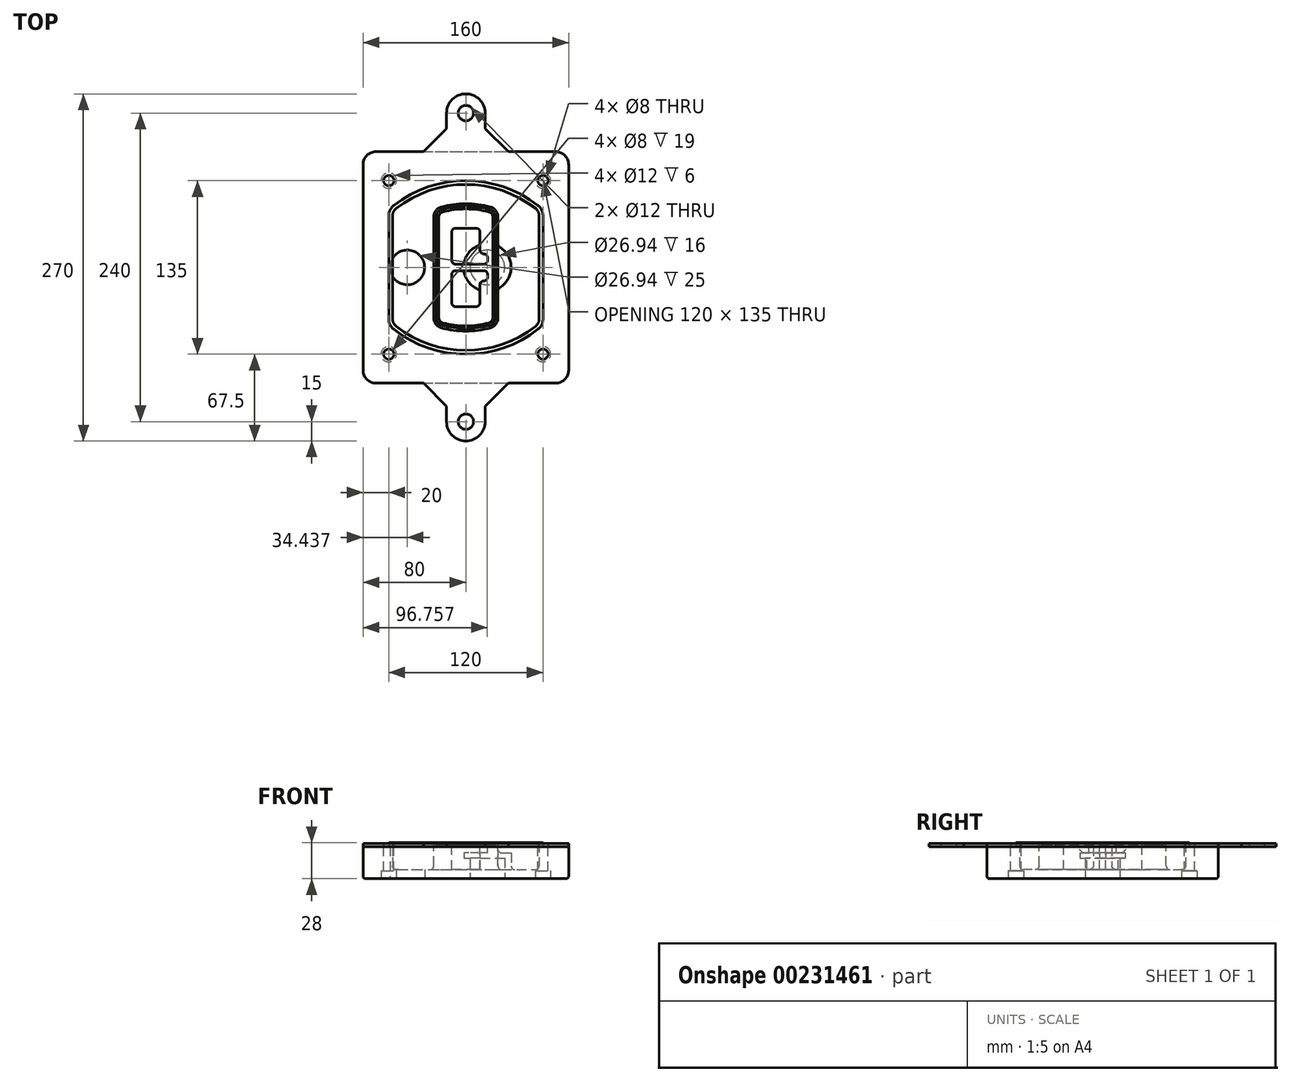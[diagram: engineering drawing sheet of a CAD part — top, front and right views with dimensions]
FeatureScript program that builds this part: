
annotation { "Feature Type Name" : "Feature", "Feature Type Description" : "" }
export const myFeature = defineFeature(function(context is Context, id is Id, definition is map)
    precondition{}
    {
        {
            var Q0;
            Q0=qCreatedBy(makeId("Top.planeOp"),FACE);
            var sketch = newSketch(context, id + "F0", { "sketchPlane" : qUnion([Q0])});
            skPoint(sketch, "E0.rect.middle", {"position": v(0, 0) * mm});
            skLineSegment(sketch, "E1.bottom", {"start": v(-70, -90) * mm, "end": v(70, -90) * mm});
            skLineSegment(sketch, "E1.top", {"start": v(-70, 90) * mm, "end": v(70, 90) * mm});
            skLineSegment(sketch, "E1.left", {"start": v(-80, -80) * mm, "end": v(-80, 80) * mm});
            skLineSegment(sketch, "E1.right", {"start": v(80, -80) * mm, "end": v(80, 80) * mm});
            skLineSegment(sketch, "E2", {"start": v(-80, 90) * mm, "end": v(80, -90) * mm, "construction": true});
            skLineSegment(sketch, "E3", {"start": v(80, 90) * mm, "end": v(-80, -90) * mm, "construction": true});
            skCircle(sketch, "E4", {"center": v(-60, 67.5) * mm, "radius": 4 * mm});
            skCircle(sketch, "E5", {"center": v(60, 67.5) * mm, "radius": 4 * mm});
            skCircle(sketch, "E6", {"center": v(60, -67.5) * mm, "radius": 4 * mm});
            skCircle(sketch, "E7", {"center": v(-60, -67.5) * mm, "radius": 4 * mm});
            skLineSegment(sketch, "E8", {"start": v(-60, 67.5) * mm, "end": v(60, 67.5) * mm, "construction": true});
            skLineSegment(sketch, "E9", {"start": v(60, 67.5) * mm, "end": v(60, -67.5) * mm, "construction": true});
            skLineSegment(sketch, "E10", {"start": v(60, -67.5) * mm, "end": v(-60, -67.5) * mm, "construction": true});
            skLineSegment(sketch, "E11", {"start": v(-60, -67.5) * mm, "end": v(-60, 67.5) * mm, "construction": true});
            skLineSegment(sketch, "E12", {"start": v(-60, 40.3) * mm, "end": v(-60, -40.3) * mm});
            skLineSegment(sketch, "E13", {"start": v(60, 40.3) * mm, "end": v(60, -40.3) * mm});
            skArc(sketch, "E14", {"start": v(56.15, 48.18) * mm, "mid": v(0, 67.5) * mm, "end": v(-56.15, 48.18) * mm});
            skArc(sketch, "E15", {"start": v(-56.15, -48.18) * mm, "mid": v(0, -67.5) * mm, "end": v(56.15, -48.18) * mm});
            skLineSegment(sketch, "E16", {"start": v(-60, 0) * mm, "end": v(60, 0) * mm, "construction": true});
            skPoint(sketch, "E17.visualSharp", {"position": v(-60, -45) * mm});
            skArc(sketch, "E17.filletArc", {"start": v(-60, -40.3) * mm, "mid": v(-58.99, -44.68) * mm, "end": v(-56.15, -48.18) * mm});
            skPoint(sketch, "E18.visualSharp", {"position": v(-60, 45) * mm});
            skArc(sketch, "E18.filletArc", {"start": v(-56.15, 48.18) * mm, "mid": v(-58.99, 44.68) * mm, "end": v(-60, 40.3) * mm});
            skPoint(sketch, "E19.visualSharp", {"position": v(60, 45) * mm});
            skArc(sketch, "E19.filletArc", {"start": v(60, 40.3) * mm, "mid": v(58.99, 44.68) * mm, "end": v(56.15, 48.18) * mm});
            skPoint(sketch, "E20.visualSharp", {"position": v(60, -45) * mm});
            skArc(sketch, "E20.filletArc", {"start": v(56.15, -48.18) * mm, "mid": v(58.99, -44.68) * mm, "end": v(60, -40.3) * mm});
            skPoint(sketch, "E21.visualSharp", {"position": v(-80, 90) * mm});
            skArc(sketch, "E21.filletArc", {"start": v(-70, 90) * mm, "mid": v(-77.07, 87.07) * mm, "end": v(-80, 80) * mm});
            skPoint(sketch, "E22.visualSharp", {"position": v(80, 90) * mm});
            skArc(sketch, "E22.filletArc", {"start": v(80, 80) * mm, "mid": v(77.07, 87.07) * mm, "end": v(70, 90) * mm});
            skPoint(sketch, "E23.visualSharp", {"position": v(80, -90) * mm});
            skArc(sketch, "E23.filletArc", {"start": v(70, -90) * mm, "mid": v(77.07, -87.07) * mm, "end": v(80, -80) * mm});
            skPoint(sketch, "E24.visualSharp", {"position": v(-80, -90) * mm});
            skArc(sketch, "E24.filletArc", {"start": v(-80, -80) * mm, "mid": v(-77.07, -87.07) * mm, "end": v(-70, -90) * mm});
            skArc(sketch, "E25.0", {"start": v(57, 40.3) * mm, "mid": v(56.3, 43.36) * mm, "end": v(54.3, 45.81) * mm});
            skLineSegment(sketch, "E25.1", {"start": v(57, 40.3) * mm, "end": v(57, -40.3) * mm});
            skArc(sketch, "E25.2", {"start": v(54.3, -45.81) * mm, "mid": v(56.3, -43.36) * mm, "end": v(57, -40.3) * mm});
            skArc(sketch, "E25.3", {"start": v(-54.3, -45.81) * mm, "mid": v(0, -64.5) * mm, "end": v(54.3, -45.81) * mm});
            skArc(sketch, "E25.4", {"start": v(-57, -40.3) * mm, "mid": v(-56.3, -43.36) * mm, "end": v(-54.3, -45.81) * mm});
            skArc(sketch, "E25.5", {"start": v(54.3, 45.81) * mm, "mid": v(0, 64.5) * mm, "end": v(-54.3, 45.81) * mm});
            skLineSegment(sketch, "E25.6", {"start": v(-57, 40.3) * mm, "end": v(-57, -40.3) * mm});
            skArc(sketch, "E25.7", {"start": v(-54.3, 45.81) * mm, "mid": v(-56.3, 43.36) * mm, "end": v(-57, 40.3) * mm});
            skArc(sketch, "E26.0", {"start": v(-58.62, 51.33) * mm, "mid": v(-62.58, 46.43) * mm, "end": v(-64, 40.3) * mm});
            skArc(sketch, "E26.1", {"start": v(58.62, 51.33) * mm, "mid": v(0, 71.5) * mm, "end": v(-58.62, 51.33) * mm});
            skArc(sketch, "E26.2", {"start": v(64, 40.3) * mm, "mid": v(62.58, 46.43) * mm, "end": v(58.62, 51.33) * mm});
            skLineSegment(sketch, "E26.3", {"start": v(64, 40.3) * mm, "end": v(64, -40.3) * mm});
            skArc(sketch, "E26.4", {"start": v(58.62, -51.33) * mm, "mid": v(62.58, -46.43) * mm, "end": v(64, -40.3) * mm});
            skLineSegment(sketch, "E26.5", {"start": v(-64, 40.3) * mm, "end": v(-64, -40.3) * mm});
            skArc(sketch, "E26.6", {"start": v(-58.62, -51.33) * mm, "mid": v(0, -71.5) * mm, "end": v(58.62, -51.33) * mm});
            skArc(sketch, "E26.7", {"start": v(-64, -40.3) * mm, "mid": v(-62.58, -46.43) * mm, "end": v(-58.62, -51.33) * mm});
            skSolve(sketch);
        }
        {
            var Q0;
            Q0=makeQuery(id+"F0.imprint","IMPRINT",FACE,{"disambiguationData":[TD([[makeQuery(id+"F0.imprint","IMPRINT",EDGE,{"derivedFrom":sQuery(id+"F0.wireOp",EDGE,"E1.bottom")}),1.0]])]});
            var Q1;
            Q1=makeQuery(id+"F0.imprint","IMPRINT",FACE,{"disambiguationData":[TD([[makeQuery(id+"F0.imprint","IMPRINT",EDGE,{"derivedFrom":sQuery(id+"F0.wireOp",EDGE,"E12")}),1.0]])]});
            var Q2;
            Q2=makeQuery(id+"F0.imprint","IMPRINT",FACE,{"disambiguationData":[TD([[makeQuery(id+"F0.imprint","IMPRINT",EDGE,{"derivedFrom":sQuery(id+"F0.wireOp",EDGE,"E25.0")}),1.0]])]});
            var Q3;
            Q3=makeQuery(id+"F0.imprint","IMPRINT",FACE,{"disambiguationData":[TD([[makeQuery(id+"F0.imprint","IMPRINT",EDGE,{"derivedFrom":sQuery(id+"F0.wireOp",EDGE,"E12")}),-1.0]])]});
            extrude(context, id + "F1", {"entities" : qUnion([Q0, Q1, Q2, Q3]), "oppositeDirection" : true, "depth" : 25 * mm});
        }
        {
            var Q0;
            Q0=makeQuery(id+"F0.imprint","IMPRINT",FACE,{"disambiguationData":[TD([[makeQuery(id+"F0.imprint","IMPRINT",EDGE,{"derivedFrom":sQuery(id+"F0.wireOp",EDGE,"E12")}),1.0]])]});
            extrude(context, id + "F2", {"entities" : qUnion([Q0]), "operationType" : NewBodyOperationType.ADD, "depth" : 3 * mm});
        }
        {
            var Q0;
            Q0=makeQuery(id+"F0.imprint","IMPRINT",FACE,{"disambiguationData":[TD([[makeQuery(id+"F0.imprint","IMPRINT",EDGE,{"derivedFrom":sQuery(id+"F0.wireOp",EDGE,"E25.0")}),1.0]])]});
            extrude(context, id + "F3", {"entities" : qUnion([Q0]), "operationType" : NewBodyOperationType.REMOVE, "oppositeDirection" : true, "depth" : 18 * mm});
        }
        {
            var Q0;
            Q0=makeQuery(id+"F2.opExtrude","CAP_FACE",FACE,{"disambiguationData":[OSD([sQuery(id+"F0.wireOp",EDGE,"E12"),sQuery(id+"F0.wireOp",EDGE,"E13"),sQuery(id+"F0.wireOp",EDGE,"E14"),sQuery(id+"F0.wireOp",EDGE,"E15"),sQuery(id+"F0.wireOp",EDGE,"E17.filletArc"),sQuery(id+"F0.wireOp",EDGE,"E18.filletArc"),sQuery(id+"F0.wireOp",EDGE,"E19.filletArc"),sQuery(id+"F0.wireOp",EDGE,"E20.filletArc"),sQuery(id+"F0.wireOp",EDGE,"E25.0"),sQuery(id+"F0.wireOp",EDGE,"E25.1"),sQuery(id+"F0.wireOp",EDGE,"E25.2"),sQuery(id+"F0.wireOp",EDGE,"E25.3"),sQuery(id+"F0.wireOp",EDGE,"E25.4"),sQuery(id+"F0.wireOp",EDGE,"E25.5"),sQuery(id+"F0.wireOp",EDGE,"E25.6"),sQuery(id+"F0.wireOp",EDGE,"E25.7")])],"isStart":false});
            var sketch = newSketch(context, id + "F4", { "sketchPlane" : qUnion([Q0])});
            skArc(sketch, "E27.0", {"start": v(-19.08, -46.97) * mm, "mid": v(0, -49.5) * mm, "end": v(19.08, -46.97) * mm});
            skArc(sketch, "E28.0", {"start": v(19.08, 46.97) * mm, "mid": v(0, 49.5) * mm, "end": v(-19.08, 46.97) * mm});
            skLineSegment(sketch, "E29", {"start": v(-25, 39.25) * mm, "end": v(-25, -39.25) * mm});
            skLineSegment(sketch, "E30", {"start": v(25, 39.25) * mm, "end": v(25, -39.25) * mm});
            skLineSegment(sketch, "E31", {"start": v(-25, 45.1) * mm, "end": v(25, 45.1) * mm, "construction": true});
            skLineSegment(sketch, "E32", {"start": v(-25, -45.1) * mm, "end": v(25, -45.1) * mm, "construction": true});
            skPoint(sketch, "E33.visualSharp", {"position": v(-25, 45.1) * mm});
            skArc(sketch, "E33.filletArc", {"start": v(-19.08, 46.97) * mm, "mid": v(-23.35, 44.11) * mm, "end": v(-25, 39.25) * mm});
            skPoint(sketch, "E34.visualSharp", {"position": v(25, 45.1) * mm});
            skArc(sketch, "E34.filletArc", {"start": v(25, 39.25) * mm, "mid": v(23.35, 44.11) * mm, "end": v(19.08, 46.97) * mm});
            skPoint(sketch, "E35.visualSharp", {"position": v(25, -45.1) * mm});
            skArc(sketch, "E35.filletArc", {"start": v(19.08, -46.97) * mm, "mid": v(23.35, -44.11) * mm, "end": v(25, -39.25) * mm});
            skPoint(sketch, "E36.visualSharp", {"position": v(-25, -45.1) * mm});
            skArc(sketch, "E36.filletArc", {"start": v(-25, -39.25) * mm, "mid": v(-23.35, -44.11) * mm, "end": v(-19.08, -46.97) * mm});
            skArc(sketch, "E37.0", {"start": v(54.3, 45.81) * mm, "mid": v(0, 64.5) * mm, "end": v(-54.3, 45.81) * mm});
            skArc(sketch, "E37.1", {"start": v(-54.3, 45.81) * mm, "mid": v(-56.3, 43.36) * mm, "end": v(-57, 40.3) * mm});
            skLineSegment(sketch, "E37.2", {"start": v(-57, 40.3) * mm, "end": v(-57, -40.3) * mm});
            skArc(sketch, "E37.3", {"start": v(-57, -40.3) * mm, "mid": v(-56.3, -43.36) * mm, "end": v(-54.3, -45.81) * mm});
            skArc(sketch, "E37.4", {"start": v(-54.3, -45.81) * mm, "mid": v(0, -64.5) * mm, "end": v(54.3, -45.81) * mm});
            skArc(sketch, "E37.5", {"start": v(54.3, -45.81) * mm, "mid": v(56.3, -43.36) * mm, "end": v(57, -40.3) * mm});
            skLineSegment(sketch, "E37.6", {"start": v(57, 40.3) * mm, "end": v(57, -40.3) * mm});
            skArc(sketch, "E37.7", {"start": v(57, 40.3) * mm, "mid": v(56.3, 43.36) * mm, "end": v(54.3, 45.81) * mm});
            skLineSegment(sketch, "E38.0", {"start": v(23, 39.25) * mm, "end": v(23, -39.25) * mm});
            skArc(sketch, "E38.1", {"start": v(18.56, -45.04) * mm, "mid": v(21.76, -42.9) * mm, "end": v(23, -39.25) * mm});
            skArc(sketch, "E38.2", {"start": v(-18.56, -45.04) * mm, "mid": v(0, -47.5) * mm, "end": v(18.56, -45.04) * mm});
            skArc(sketch, "E38.3", {"start": v(-23, -39.25) * mm, "mid": v(-21.76, -42.9) * mm, "end": v(-18.56, -45.04) * mm});
            skLineSegment(sketch, "E38.4", {"start": v(-23, 39.25) * mm, "end": v(-23, -39.25) * mm});
            skArc(sketch, "E38.5", {"start": v(23, 39.25) * mm, "mid": v(21.76, 42.9) * mm, "end": v(18.56, 45.04) * mm});
            skArc(sketch, "E38.6", {"start": v(-18.56, 45.04) * mm, "mid": v(-21.76, 42.9) * mm, "end": v(-23, 39.25) * mm});
            skArc(sketch, "E38.7", {"start": v(18.56, 45.04) * mm, "mid": v(0, 47.5) * mm, "end": v(-18.56, 45.04) * mm});
            skArc(sketch, "E39.0", {"start": v(21, 39.25) * mm, "mid": v(20.18, 41.68) * mm, "end": v(18.04, 43.1) * mm});
            skLineSegment(sketch, "E39.1", {"start": v(21, 39.25) * mm, "end": v(21, -39.25) * mm});
            skArc(sketch, "E39.2", {"start": v(18.04, -43.1) * mm, "mid": v(20.18, -41.68) * mm, "end": v(21, -39.25) * mm});
            skArc(sketch, "E39.3", {"start": v(-18.04, -43.1) * mm, "mid": v(0, -45.5) * mm, "end": v(18.04, -43.1) * mm});
            skArc(sketch, "E39.4", {"start": v(-21, -39.25) * mm, "mid": v(-20.18, -41.68) * mm, "end": v(-18.04, -43.1) * mm});
            skArc(sketch, "E39.5", {"start": v(18.04, 43.1) * mm, "mid": v(0, 45.5) * mm, "end": v(-18.04, 43.1) * mm});
            skLineSegment(sketch, "E39.6", {"start": v(-21, 39.25) * mm, "end": v(-21, -39.25) * mm});
            skArc(sketch, "E39.7", {"start": v(-18.04, 43.1) * mm, "mid": v(-20.18, 41.68) * mm, "end": v(-21, 39.25) * mm});
            skLineSegment(sketch, "E40", {"start": v(-25, 0) * mm, "end": v(25, 0) * mm, "construction": true});
            skLineSegment(sketch, "E41", {"start": v(-11, 5.5) * mm, "end": v(-11, 27.5) * mm});
            skLineSegment(sketch, "E42", {"start": v(-8, 30.5) * mm, "end": v(8, 30.5) * mm});
            skLineSegment(sketch, "E43", {"start": v(11, 27.5) * mm, "end": v(11, 13.5) * mm});
            skLineSegment(sketch, "E44", {"start": v(14, 10.5) * mm, "end": v(14, 10.5) * mm});
            skLineSegment(sketch, "E45", {"start": v(17, 7.5) * mm, "end": v(17, 5.5) * mm});
            skLineSegment(sketch, "E46", {"start": v(14, 2.5) * mm, "end": v(-8, 2.5) * mm});
            skPoint(sketch, "E47.visualSharp", {"position": v(-11, 30.5) * mm});
            skArc(sketch, "E47.filletArc", {"start": v(-8, 30.5) * mm, "mid": v(-10.12, 29.62) * mm, "end": v(-11, 27.5) * mm});
            skPoint(sketch, "E48.visualSharp", {"position": v(11, 30.5) * mm});
            skArc(sketch, "E48.filletArc", {"start": v(11, 27.5) * mm, "mid": v(10.12, 29.62) * mm, "end": v(8, 30.5) * mm});
            skPoint(sketch, "E49.visualSharp", {"position": v(11, 10.5) * mm});
            skArc(sketch, "E49.filletArc", {"start": v(11, 13.5) * mm, "mid": v(11.88, 11.38) * mm, "end": v(14, 10.5) * mm});
            skPoint(sketch, "E50.visualSharp", {"position": v(17, 10.5) * mm});
            skArc(sketch, "E50.filletArc", {"start": v(17, 7.5) * mm, "mid": v(16.12, 9.62) * mm, "end": v(14, 10.5) * mm});
            skPoint(sketch, "E51.visualSharp", {"position": v(17, 2.5) * mm});
            skArc(sketch, "E51.filletArc", {"start": v(14, 2.5) * mm, "mid": v(16.12, 3.38) * mm, "end": v(17, 5.5) * mm});
            skPoint(sketch, "E52.visualSharp", {"position": v(-11, 2.5) * mm});
            skArc(sketch, "E52.filletArc", {"start": v(-11, 5.5) * mm, "mid": v(-10.12, 3.38) * mm, "end": v(-8, 2.5) * mm});
            skLineSegment(sketch, "E53.0.MirrorCS", {"start": v(14, -2.5) * mm, "end": v(-8, -2.5) * mm});
            skArc(sketch, "E54.0.MirrorCS", {"start": v(-11, -5.5) * mm, "mid": v(-10.12, -3.38) * mm, "end": v(-8, -2.5) * mm});
            skLineSegment(sketch, "E55.0.MirrorCS", {"start": v(-11, -5.5) * mm, "end": v(-11, -27.5) * mm});
            skArc(sketch, "E56.0.MirrorCS", {"start": v(-8, -30.5) * mm, "mid": v(-10.12, -29.62) * mm, "end": v(-11, -27.5) * mm});
            skLineSegment(sketch, "E57.0.MirrorCS", {"start": v(-8, -30.5) * mm, "end": v(8, -30.5) * mm});
            skArc(sketch, "E58.0.MirrorCS", {"start": v(11, -27.5) * mm, "mid": v(10.12, -29.62) * mm, "end": v(8, -30.5) * mm});
            skLineSegment(sketch, "E59.0.MirrorCS", {"start": v(11, -27.5) * mm, "end": v(11, -13.5) * mm});
            skArc(sketch, "E60.0.MirrorCS", {"start": v(11, -13.5) * mm, "mid": v(11.88, -11.38) * mm, "end": v(14, -10.5) * mm});
            skArc(sketch, "E61.0.MirrorCS", {"start": v(17, -7.5) * mm, "mid": v(16.12, -9.62) * mm, "end": v(14, -10.5) * mm});
            skLineSegment(sketch, "E62.0.MirrorCS", {"start": v(17, -7.5) * mm, "end": v(17, -5.5) * mm});
            skArc(sketch, "E63.0.MirrorCS", {"start": v(14, -2.5) * mm, "mid": v(16.12, -3.38) * mm, "end": v(17, -5.5) * mm});
            skSolve(sketch);
        }
        {
            var Q0;
            Q0=makeQuery(id+"F4.imprint","IMPRINT",FACE,{"disambiguationData":[TD([[makeQuery(id+"F4.imprint","IMPRINT",EDGE,{"derivedFrom":sQuery(id+"F4.wireOp",EDGE,"E27.0")}),1.0]])]});
            var Q1;
            Q1=makeQuery(id+"F4.imprint","IMPRINT",FACE,{"disambiguationData":[TD([[makeQuery(id+"F4.imprint","IMPRINT",EDGE,{"derivedFrom":sQuery(id+"F4.wireOp",EDGE,"E38.0")}),-1.0]])]});
            var Q2;
            Q2=makeQuery(id+"F4.imprint","IMPRINT",FACE,{"disambiguationData":[TD([[makeQuery(id+"F4.imprint","IMPRINT",EDGE,{"derivedFrom":sQuery(id+"F4.wireOp",EDGE,"E39.0")}),1.0]])]});
            extrude(context, id + "F5", {"entities" : qUnion([Q0, Q1, Q2]), "operationType" : NewBodyOperationType.ADD, "endBound" : BoundingType.UP_TO_NEXT, "oppositeDirection" : true, "depth" : 25 * mm});
        }
        {
            var Q0;
            Q0=makeQuery(id+"F4.imprint","IMPRINT",FACE,{"disambiguationData":[TD([[makeQuery(id+"F4.imprint","IMPRINT",EDGE,{"derivedFrom":sQuery(id+"F4.wireOp",EDGE,"E38.0")}),-1.0]])]});
            extrude(context, id + "F6", {"entities" : qUnion([Q0]), "operationType" : NewBodyOperationType.REMOVE, "oppositeDirection" : true, "depth" : 2 * mm});
        }
        {
            var Q0;
            Q0=makeQuery(id+"F1.opExtrude","CAP_FACE",FACE,{"disambiguationData":[OSD([sQuery(id+"F0.wireOp",EDGE,"E1.bottom"),sQuery(id+"F0.wireOp",EDGE,"E1.top"),sQuery(id+"F0.wireOp",EDGE,"E1.left"),sQuery(id+"F0.wireOp",EDGE,"E1.right"),sQuery(id+"F0.wireOp",EDGE,"E4"),sQuery(id+"F0.wireOp",EDGE,"E5"),sQuery(id+"F0.wireOp",EDGE,"E6"),sQuery(id+"F0.wireOp",EDGE,"E7"),sQuery(id+"F0.wireOp",EDGE,"E21.filletArc"),sQuery(id+"F0.wireOp",EDGE,"E22.filletArc"),sQuery(id+"F0.wireOp",EDGE,"E23.filletArc"),sQuery(id+"F0.wireOp",EDGE,"E24.filletArc")])],"isStart":false});
            var sketch = newSketch(context, id + "F7", { "sketchPlane" : qUnion([Q0])});
            skCircle(sketch, "E64", {"center": v(16.76, 0) * mm, "radius": 13.47 * mm});
            skCircle(sketch, "E65", {"center": v(-45.56, 0) * mm, "radius": 13.47 * mm});
            skLineSegment(sketch, "E66", {"start": v(80, 0) * mm, "end": v(-80, 0) * mm});
            skCircle(sketch, "E67", {"center": v(16.76, 0) * mm, "radius": 18.47 * mm});
            skCircle(sketch, "E68", {"center": v(60, -67.5) * mm, "radius": 6 * mm});
            skCircle(sketch, "E69", {"center": v(-60, -67.5) * mm, "radius": 6 * mm});
            skCircle(sketch, "E70", {"center": v(-60, 67.5) * mm, "radius": 6 * mm});
            skCircle(sketch, "E71", {"center": v(60, 67.5) * mm, "radius": 6 * mm});
            skSolve(sketch);
        }
        {
            var Q0;
            {var subQ1=sQuery(id+"F7.wireOp",EDGE,"E66");var subQ4=sQuery(id+"F7.wireOp",EDGE,"E64");var subQ6=makeQuery(id+"F7.imprint","INTERSECT",VERTEX,{"disambiguationData":[OD(0.0)],"derivedFrom":[subQ4,subQ1]});Q0=makeQuery(id+"F7.imprint","IMPRINT",FACE,{"disambiguationData":[TD([[makeQuery(id+"F7.imprint","IMPRINT",EDGE,{"disambiguationData":[TD([[subQ6,-1.0]])],"derivedFrom":subQ4}),-1.0]])]});}
            var Q1;
            {var subQ0=sQuery(id+"F7.wireOp",EDGE,"E66");var subQ1=sQuery(id+"F7.wireOp",EDGE,"E64");var subQ3=makeQuery(id+"F7.imprint","INTERSECT",VERTEX,{"disambiguationData":[OD(0.0)],"derivedFrom":[subQ1,subQ0]});Q1=makeQuery(id+"F7.imprint","IMPRINT",FACE,{"disambiguationData":[TD([[makeQuery(id+"F7.imprint","IMPRINT",EDGE,{"disambiguationData":[TD([[subQ3,-1.0]])],"derivedFrom":subQ1}),1.0]])]});}
            var Q2;
            {var subQ0=sQuery(id+"F7.wireOp",EDGE,"E66");var subQ1=sQuery(id+"F7.wireOp",EDGE,"E64");var subQ3=makeQuery(id+"F7.imprint","INTERSECT",VERTEX,{"disambiguationData":[OD(0.0)],"derivedFrom":[subQ1,subQ0]});Q2=makeQuery(id+"F7.imprint","IMPRINT",FACE,{"disambiguationData":[TD([[makeQuery(id+"F7.imprint","IMPRINT",EDGE,{"disambiguationData":[TD([[subQ3,1.0]])],"derivedFrom":subQ1}),1.0]])]});}
            var Q3;
            {var subQ1=sQuery(id+"F7.wireOp",EDGE,"E66");var subQ4=sQuery(id+"F7.wireOp",EDGE,"E64");var subQ6=makeQuery(id+"F7.imprint","INTERSECT",VERTEX,{"disambiguationData":[OD(0.0)],"derivedFrom":[subQ4,subQ1]});Q3=makeQuery(id+"F7.imprint","IMPRINT",FACE,{"disambiguationData":[TD([[makeQuery(id+"F7.imprint","IMPRINT",EDGE,{"disambiguationData":[TD([[subQ6,1.0]])],"derivedFrom":subQ4}),-1.0]])]});}
            extrude(context, id + "F8", {"entities" : qUnion([Q0, Q1, Q2, Q3]), "operationType" : NewBodyOperationType.ADD, "oppositeDirection" : true, "depth" : 20 * mm});
        }
        {
            var Q0;
            {var subQ0=sQuery(id+"F7.wireOp",EDGE,"E66");var subQ1=sQuery(id+"F7.wireOp",EDGE,"E64");var subQ3=makeQuery(id+"F7.imprint","INTERSECT",VERTEX,{"disambiguationData":[OD(0.0)],"derivedFrom":[subQ1,subQ0]});Q0=makeQuery(id+"F7.imprint","IMPRINT",FACE,{"disambiguationData":[TD([[makeQuery(id+"F7.imprint","IMPRINT",EDGE,{"disambiguationData":[TD([[subQ3,-1.0]])],"derivedFrom":subQ1}),1.0]])]});}
            var Q1;
            {var subQ0=sQuery(id+"F7.wireOp",EDGE,"E66");var subQ1=sQuery(id+"F7.wireOp",EDGE,"E64");var subQ3=makeQuery(id+"F7.imprint","INTERSECT",VERTEX,{"disambiguationData":[OD(0.0)],"derivedFrom":[subQ1,subQ0]});Q1=makeQuery(id+"F7.imprint","IMPRINT",FACE,{"disambiguationData":[TD([[makeQuery(id+"F7.imprint","IMPRINT",EDGE,{"disambiguationData":[TD([[subQ3,1.0]])],"derivedFrom":subQ1}),1.0]])]});}
            extrude(context, id + "F9", {"entities" : qUnion([Q0, Q1]), "operationType" : NewBodyOperationType.REMOVE, "oppositeDirection" : true, "depth" : 16 * mm});
        }
        {
            var Q0;
            {var subQ0=sQuery(id+"F7.wireOp",EDGE,"E66");var subQ1=sQuery(id+"F7.wireOp",EDGE,"E65");var subQ3=makeQuery(id+"F7.imprint","INTERSECT",VERTEX,{"disambiguationData":[OD(0.0)],"derivedFrom":[subQ1,subQ0]});Q0=makeQuery(id+"F7.imprint","IMPRINT",FACE,{"disambiguationData":[TD([[makeQuery(id+"F7.imprint","IMPRINT",EDGE,{"disambiguationData":[TD([[subQ3,-1.0]])],"derivedFrom":subQ1}),1.0]])]});}
            var Q1;
            {var subQ0=sQuery(id+"F7.wireOp",EDGE,"E66");var subQ1=sQuery(id+"F7.wireOp",EDGE,"E65");var subQ3=makeQuery(id+"F7.imprint","INTERSECT",VERTEX,{"disambiguationData":[OD(0.0)],"derivedFrom":[subQ1,subQ0]});Q1=makeQuery(id+"F7.imprint","IMPRINT",FACE,{"disambiguationData":[TD([[makeQuery(id+"F7.imprint","IMPRINT",EDGE,{"disambiguationData":[TD([[subQ3,1.0]])],"derivedFrom":subQ1}),1.0]])]});}
            extrude(context, id + "F10", {"entities" : qUnion([Q0, Q1]), "operationType" : NewBodyOperationType.REMOVE, "oppositeDirection" : true, "depth" : 25 * mm});
        }
        {
            var Q0;
            Q0=makeQuery(id+"F7.imprint","IMPRINT",FACE,{"disambiguationData":[TD([[makeQuery(id+"F7.imprint","IMPRINT",EDGE,{"derivedFrom":sQuery(id+"F7.wireOp",EDGE,"E68")}),1.0]])]});
            var Q1;
            Q1=makeQuery(id+"F7.imprint","IMPRINT",FACE,{"disambiguationData":[TD([[makeQuery(id+"F7.imprint","IMPRINT",EDGE,{"derivedFrom":makeQuery(id+"F1.opExtrude","CAP_EDGE",EDGE,{"disambiguationData":[OSD([sQuery(id+"F0.wireOp",EDGE,"E5")])],"isStart":false})}),-1.0]])]});
            var Q2;
            Q2=makeQuery(id+"F7.imprint","IMPRINT",FACE,{"disambiguationData":[TD([[makeQuery(id+"F7.imprint","IMPRINT",EDGE,{"derivedFrom":sQuery(id+"F7.wireOp",EDGE,"E69")}),1.0]])]});
            var Q3;
            Q3=makeQuery(id+"F7.imprint","IMPRINT",FACE,{"disambiguationData":[TD([[makeQuery(id+"F7.imprint","IMPRINT",EDGE,{"derivedFrom":makeQuery(id+"F1.opExtrude","CAP_EDGE",EDGE,{"disambiguationData":[OSD([sQuery(id+"F0.wireOp",EDGE,"E4")])],"isStart":false})}),-1.0]])]});
            var Q4;
            Q4=makeQuery(id+"F7.imprint","IMPRINT",FACE,{"disambiguationData":[TD([[makeQuery(id+"F7.imprint","IMPRINT",EDGE,{"derivedFrom":sQuery(id+"F7.wireOp",EDGE,"E70")}),1.0]])]});
            var Q5;
            Q5=makeQuery(id+"F7.imprint","IMPRINT",FACE,{"disambiguationData":[TD([[makeQuery(id+"F7.imprint","IMPRINT",EDGE,{"derivedFrom":makeQuery(id+"F1.opExtrude","CAP_EDGE",EDGE,{"disambiguationData":[OSD([sQuery(id+"F0.wireOp",EDGE,"E7")])],"isStart":false})}),-1.0]])]});
            var Q6;
            Q6=makeQuery(id+"F7.imprint","IMPRINT",FACE,{"disambiguationData":[TD([[makeQuery(id+"F7.imprint","IMPRINT",EDGE,{"derivedFrom":sQuery(id+"F7.wireOp",EDGE,"E71")}),1.0]])]});
            var Q7;
            Q7=makeQuery(id+"F7.imprint","IMPRINT",FACE,{"disambiguationData":[TD([[makeQuery(id+"F7.imprint","IMPRINT",EDGE,{"derivedFrom":makeQuery(id+"F1.opExtrude","CAP_EDGE",EDGE,{"disambiguationData":[OSD([sQuery(id+"F0.wireOp",EDGE,"E6")])],"isStart":false})}),-1.0]])]});
            extrude(context, id + "F11", {"entities" : qUnion([Q0, Q1, Q2, Q3, Q4, Q5, Q6, Q7]), "operationType" : NewBodyOperationType.REMOVE, "oppositeDirection" : true, "depth" : 6 * mm});
        }
        {
            var Q0;
            Q0=makeQuery(id+"F9.boolean.opBoolean","COPY",FACE,{"derivedFrom":makeQuery(id+"F9.opExtrude","CAP_FACE",FACE,{"disambiguationData":[OSD([sQuery(id+"F7.wireOp",EDGE,"E64")])],"isStart":false})});
            var sketch = newSketch(context, id + "F12", { "sketchPlane" : qUnion([Q0])});
            skArc(sketch, "E72.0", {"start": v(11, 17.55) * mm, "mid": v(2.57, 11.82) * mm, "end": v(-1.54, 2.5) * mm});
            skArc(sketch, "E72.1", {"start": v(-1.54, -2.5) * mm, "mid": v(2.57, -11.82) * mm, "end": v(11, -17.55) * mm});
            skLineSegment(sketch, "E73", {"start": v(-1.54, -2.5) * mm, "end": v(14, -2.5) * mm});
            skLineSegment(sketch, "E74.0", {"start": v(14, 2.5) * mm, "end": v(-1.54, 2.5) * mm});
            skArc(sketch, "E74.1", {"start": v(14, 2.5) * mm, "mid": v(16.12, 3.38) * mm, "end": v(17, 5.5) * mm});
            skLineSegment(sketch, "E74.2", {"start": v(17, 7.5) * mm, "end": v(17, 5.5) * mm});
            skArc(sketch, "E74.3", {"start": v(17, 7.5) * mm, "mid": v(16.12, 9.62) * mm, "end": v(14, 10.5) * mm});
            skArc(sketch, "E74.4", {"start": v(11, 13.5) * mm, "mid": v(11.88, 11.38) * mm, "end": v(14, 10.5) * mm});
            skLineSegment(sketch, "E74.5", {"start": v(11, 17.55) * mm, "end": v(11, 13.5) * mm});
            skLineSegment(sketch, "E74.7", {"start": v(14, -2.5) * mm, "end": v(-1.54, -2.5) * mm});
            skArc(sketch, "E74.8", {"start": v(14, -2.5) * mm, "mid": v(16.12, -3.38) * mm, "end": v(17, -5.5) * mm});
            skLineSegment(sketch, "E74.9", {"start": v(17, -7.5) * mm, "end": v(17, -5.5) * mm});
            skArc(sketch, "E74.10", {"start": v(17, -7.5) * mm, "mid": v(16.12, -9.62) * mm, "end": v(14, -10.5) * mm});
            skArc(sketch, "E74.11", {"start": v(11, -13.5) * mm, "mid": v(11.88, -11.38) * mm, "end": v(14, -10.5) * mm});
            skLineSegment(sketch, "E74.12", {"start": v(11, -17.55) * mm, "end": v(11, -13.5) * mm});
            skPoint(sketch, "E75.orphan", {"position": v(11, -27.5) * mm});
            skPoint(sketch, "E76.orphan", {"position": v(-8, -2.5) * mm});
            skPoint(sketch, "E77.orphan", {"position": v(-8, 2.5) * mm});
            skPoint(sketch, "E78.orphan", {"position": v(11, 27.5) * mm});
            skSolve(sketch);
        }
        {
            var Q0;
            {var subQ7=sQuery(id+"F12.wireOp",EDGE,"E72.0");var subQ14=sQuery(id+"F12.wireOp",EDGE,"E72.1");var subQ16=sQuery(id+"F12.wireOp",EDGE,"E74.1");var subQ18=sQuery(id+"F12.wireOp",EDGE,"E74.8");Q0=qUnion([makeQuery(id+"F12.imprint","IMPRINT",FACE,{"disambiguationData":[TD([[makeQuery(id+"F12.imprint","IMPRINT",EDGE,{"derivedFrom":subQ7}),1.0]])]}),makeQuery(id+"F12.imprint","IMPRINT",FACE,{"disambiguationData":[TD([[makeQuery(id+"F12.imprint","IMPRINT",EDGE,{"derivedFrom":subQ14}),1.0]])]}),makeQuery(id+"F12.imprint","IMPRINT",FACE,{"disambiguationData":[TD([[makeQuery(id+"F12.imprint","IMPRINT",EDGE,{"derivedFrom":subQ16}),1.0]])]}),makeQuery(id+"F12.imprint","IMPRINT",FACE,{"disambiguationData":[TD([[makeQuery(id+"F12.imprint","IMPRINT",EDGE,{"derivedFrom":subQ18}),-1.0]])]})]);}
            var Q1;
            Q1=makeQuery(id+"F5.boolean.opBoolean","SPLIT",FACE,{"disambiguationData":[TD([makeQuery(id+"F5.opExtrude","SWEPT_FACE",FACE,{"disambiguationData":[OSD([sQuery(id+"F4.wireOp",EDGE,"E41")])]})])],"derivedFrom":makeQuery(id+"F3.boolean.opBoolean","COPY",FACE,{"derivedFrom":makeQuery(id+"F3.opExtrude","CAP_FACE",FACE,{"disambiguationData":[OSD([sQuery(id+"F0.wireOp",EDGE,"E25.0"),sQuery(id+"F0.wireOp",EDGE,"E25.1"),sQuery(id+"F0.wireOp",EDGE,"E25.2"),sQuery(id+"F0.wireOp",EDGE,"E25.3"),sQuery(id+"F0.wireOp",EDGE,"E25.4"),sQuery(id+"F0.wireOp",EDGE,"E25.5"),sQuery(id+"F0.wireOp",EDGE,"E25.6"),sQuery(id+"F0.wireOp",EDGE,"E25.7")])],"isStart":false})})});
            extrude(context, id + "F13", {"entities" : qUnion([Q0]), "operationType" : NewBodyOperationType.REMOVE, "endBound" : BoundingType.UP_TO_SURFACE, "endBoundEntityFace" : qUnion([Q1]), "depth" : 25 * mm});
        }
        {
            var Q0;
            Q0=makeQuery(id+"F3.boolean.opBoolean","COPY",EDGE,{"derivedFrom":makeQuery(id+"F3.opExtrude","CAP_EDGE",EDGE,{"disambiguationData":[OSD([sQuery(id+"F0.wireOp",EDGE,"E25.6")])],"isStart":false})});
            var Q1;
            Q1=makeQuery(id+"F8.boolean.opBoolean","INTERSECT",EDGE,{"derivedFrom":[makeQuery(id+"F5.opExtrude","SWEPT_FACE",FACE,{"disambiguationData":[OSD([sQuery(id+"F4.wireOp",EDGE,"E30")])]}),makeQuery(id+"F8.opExtrude","CAP_FACE",FACE,{"disambiguationData":[OSD([sQuery(id+"F7.wireOp",EDGE,"E67")])],"isStart":false})]});
            var Q2;
            Q2=makeQuery(id+"F8.boolean.opBoolean","INTERSECT",EDGE,{"disambiguationData":[OD(1.0)],"derivedFrom":[makeQuery(id+"F5.opExtrude","SWEPT_FACE",FACE,{"disambiguationData":[OSD([sQuery(id+"F4.wireOp",EDGE,"E30")])]}),makeQuery(id+"F8.opExtrude","SWEPT_FACE",FACE,{"disambiguationData":[OSD([sQuery(id+"F7.wireOp",EDGE,"E67")])]})]});
            var Q3;
            {var subQ0=sQuery(id+"F4.wireOp",EDGE,"E30");Q3=makeQuery(id+"F8.boolean.opBoolean","SPLIT",EDGE,{"disambiguationData":[TD([makeQuery(id+"F5.opExtrude","SWEPT_FACE",FACE,{"disambiguationData":[OSD([sQuery(id+"F4.wireOp",EDGE,"E35.filletArc")])]})])],"derivedFrom":makeQuery(id+"F5.opExtrude","CAP_EDGE",EDGE,{"disambiguationData":[OSD([subQ0])],"isStart":false})});}
            var Q4;
            {var subQ0=sQuery(id+"F0.wireOp",EDGE,"E25.7");var subQ1=sQuery(id+"F0.wireOp",EDGE,"E25.1");var subQ2=sQuery(id+"F0.wireOp",EDGE,"E25.6");var subQ3=sQuery(id+"F0.wireOp",EDGE,"E25.5");var subQ4=sQuery(id+"F0.wireOp",EDGE,"E25.4");var subQ5=sQuery(id+"F0.wireOp",EDGE,"E25.0");var subQ6=sQuery(id+"F0.wireOp",EDGE,"E25.2");var subQ7=sQuery(id+"F0.wireOp",EDGE,"E25.3");Q4=makeQuery(id+"F8.boolean.opBoolean","INTERSECT",EDGE,{"derivedFrom":[makeQuery(id+"F5.boolean.opBoolean","SPLIT",FACE,{"disambiguationData":[TD([makeQuery(id+"F2.opExtrude","SWEPT_FACE",FACE,{"disambiguationData":[OSD([subQ5])]})])],"derivedFrom":makeQuery(id+"F3.boolean.opBoolean","COPY",FACE,{"derivedFrom":makeQuery(id+"F3.opExtrude","CAP_FACE",FACE,{"disambiguationData":[OSD([subQ5,subQ1,subQ6,subQ7,subQ4,subQ3,subQ2,subQ0])],"isStart":false})})}),makeQuery(id+"F8.opExtrude","SWEPT_FACE",FACE,{"disambiguationData":[OSD([sQuery(id+"F7.wireOp",EDGE,"E67")])]})]});}
            var Q5;
            Q5=makeQuery(id+"F8.boolean.opBoolean","INTERSECT",EDGE,{"disambiguationData":[OD(0.0)],"derivedFrom":[makeQuery(id+"F5.opExtrude","SWEPT_FACE",FACE,{"disambiguationData":[OSD([sQuery(id+"F4.wireOp",EDGE,"E30")])]}),makeQuery(id+"F8.opExtrude","SWEPT_FACE",FACE,{"disambiguationData":[OSD([sQuery(id+"F7.wireOp",EDGE,"E67")])]})]});
            fillet(context, id + "F14", {"entities" : qUnion([Q0, Q1, Q2, Q3, Q4, Q5]), "radius" : 3 * mm, "tangentPropagation" : true, "allowEdgeOverflow" : false});
        }
        {
            var Q0;
            Q0=makeQuery(id+"F1.opExtrude","CAP_EDGE",EDGE,{"disambiguationData":[OSD([sQuery(id+"F0.wireOp",EDGE,"E1.bottom")])],"isStart":false});
            fillet(context, id + "F15", {"entities" : qUnion([Q0]), "radius" : 2 * mm, "tangentPropagation" : true, "allowEdgeOverflow" : false});
        }
        {
            var Q0;
            {var subQ0=sQuery(id+"F0.wireOp",EDGE,"E22.filletArc");var subQ1=sQuery(id+"F0.wireOp",EDGE,"E7");var subQ2=sQuery(id+"F0.wireOp",EDGE,"E6");var subQ3=sQuery(id+"F0.wireOp",EDGE,"E5");var subQ4=sQuery(id+"F0.wireOp",EDGE,"E4");var subQ5=sQuery(id+"F0.wireOp",EDGE,"E1.bottom");var subQ6=sQuery(id+"F0.wireOp",EDGE,"E21.filletArc");var subQ7=sQuery(id+"F0.wireOp",EDGE,"E1.top");var subQ8=sQuery(id+"F0.wireOp",EDGE,"E1.left");var subQ9=sQuery(id+"F0.wireOp",EDGE,"E1.right");var subQ10=sQuery(id+"F0.wireOp",EDGE,"E23.filletArc");var subQ11=sQuery(id+"F0.wireOp",EDGE,"E24.filletArc");Q0=makeQuery(id+"F2.boolean.opBoolean","SPLIT",FACE,{"disambiguationData":[TD([makeQuery(id+"F1.opExtrude","SWEPT_FACE",FACE,{"disambiguationData":[OSD([subQ5])]})])],"derivedFrom":makeQuery(id+"F1.opExtrude","CAP_FACE",FACE,{"disambiguationData":[OSD([subQ5,subQ7,subQ8,subQ9,subQ4,subQ3,subQ2,subQ1,subQ6,subQ0,subQ10,subQ11])],"isStart":true})});}
            var sketch = newSketch(context, id + "F16", { "sketchPlane" : qUnion([Q0])});
            skLineSegment(sketch, "E79.0", {"start": v(-70, 90) * mm, "end": v(70, 90) * mm});
            skCircle(sketch, "E79.2", {"center": v(-60, 67.5) * mm, "radius": 4 * mm});
            skLineSegment(sketch, "E79.3", {"start": v(-80, -80) * mm, "end": v(-80, 80) * mm});
            skCircle(sketch, "E79.4", {"center": v(60, 67.5) * mm, "radius": 4 * mm});
            skArc(sketch, "E79.5", {"start": v(80, 80) * mm, "mid": v(77.07, 87.07) * mm, "end": v(70, 90) * mm});
            skLineSegment(sketch, "E79.6", {"start": v(80, -80) * mm, "end": v(80, 80) * mm});
            skCircle(sketch, "E79.7", {"center": v(60, -67.5) * mm, "radius": 4 * mm});
            skLineSegment(sketch, "E79.8", {"start": v(-70, -90) * mm, "end": v(70, -90) * mm});
            skArc(sketch, "E79.9", {"start": v(-80, -80) * mm, "mid": v(-77.07, -87.07) * mm, "end": v(-70, -90) * mm});
            skCircle(sketch, "E79.10", {"center": v(-60, -67.5) * mm, "radius": 4 * mm});
            skLineSegment(sketch, "E79.11", {"start": v(-60, 40.3) * mm, "end": v(-60, -40.3) * mm});
            skPoint(sketch, "E79.12", {"position": v(-56.15, 48.18) * mm});
            skArc(sketch, "E79.13", {"start": v(56.15, 48.18) * mm, "mid": v(0, 67.5) * mm, "end": v(-56.15, 48.18) * mm});
            skArc(sketch, "E79.14", {"start": v(60, 40.3) * mm, "mid": v(58.99, 44.68) * mm, "end": v(56.15, 48.18) * mm});
            skArc(sketch, "E79.15", {"start": v(-56.15, -48.18) * mm, "mid": v(0, -67.5) * mm, "end": v(56.15, -48.18) * mm});
            skArc(sketch, "E79.16", {"start": v(56.15, -48.18) * mm, "mid": v(58.99, -44.68) * mm, "end": v(60, -40.3) * mm});
            skArc(sketch, "E79.17", {"start": v(-60, -40.3) * mm, "mid": v(-58.99, -44.68) * mm, "end": v(-56.15, -48.18) * mm});
            skLineSegment(sketch, "E79.18", {"start": v(60, 40.3) * mm, "end": v(60, -40.3) * mm});
            skArc(sketch, "E79.19", {"start": v(-56.15, 48.18) * mm, "mid": v(-58.99, 44.68) * mm, "end": v(-60, 40.3) * mm});
            skArc(sketch, "E79.20", {"start": v(70, -90) * mm, "mid": v(77.07, -87.07) * mm, "end": v(80, -80) * mm});
            skArc(sketch, "E79.21", {"start": v(-70, 90) * mm, "mid": v(-77.07, 87.07) * mm, "end": v(-80, 80) * mm});
            skPoint(sketch, "E79.22", {"position": v(-77.07, 87.07) * mm});
            skPoint(sketch, "E79.23", {"position": v(77.07, -87.07) * mm});
            skPoint(sketch, "E79.24", {"position": v(-58.99, 44.68) * mm});
            skCircle(sketch, "E80", {"center": v(0, 120) * mm, "radius": 6 * mm});
            skArc(sketch, "E81", {"start": v(15, 120) * mm, "mid": v(0, 135) * mm, "end": v(-15, 120) * mm});
            skLineSegment(sketch, "E82", {"start": v(-15, 120) * mm, "end": v(-15, 108) * mm});
            skLineSegment(sketch, "E83", {"start": v(15, 120) * mm, "end": v(15, 108) * mm});
            skLineSegment(sketch, "E84", {"start": v(-15, 108) * mm, "end": v(-33, 90) * mm});
            skLineSegment(sketch, "E85", {"start": v(15, 108) * mm, "end": v(33, 90) * mm});
            skLineSegment(sketch, "E86", {"start": v(0, 120) * mm, "end": v(0, 90) * mm, "construction": true});
            skLineSegment(sketch, "E87", {"start": v(-80, 0) * mm, "end": v(80, 0) * mm, "construction": true});
            skLineSegment(sketch, "E88.MirrorCS", {"start": v(0, -120) * mm, "end": v(0, -90) * mm, "construction": true});
            skCircle(sketch, "E89.MirrorC", {"center": v(0, -120) * mm, "radius": 6 * mm});
            skArc(sketch, "E90.MirrorCS", {"start": v(15, -120) * mm, "mid": v(0, -135) * mm, "end": v(-15, -120) * mm});
            skLineSegment(sketch, "E91.MirrorCS", {"start": v(15, -120) * mm, "end": v(15, -108) * mm});
            skLineSegment(sketch, "E92.MirrorCS", {"start": v(15, -108) * mm, "end": v(33, -90) * mm});
            skLineSegment(sketch, "E93.MirrorCS", {"start": v(-15, -108) * mm, "end": v(-33, -90) * mm});
            skLineSegment(sketch, "E94.MirrorCS", {"start": v(-15, -120) * mm, "end": v(-15, -108) * mm});
            skSolve(sketch);
        }
        {
            var Q0;
            Q0 = qSketchRegion(id + "F16", true);
            extrude(context, id + "F17", {"entities" : qUnion([Q0]), "depth" : 2.5 * mm});
        }
    });
